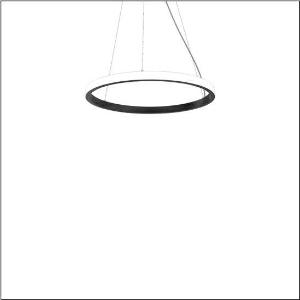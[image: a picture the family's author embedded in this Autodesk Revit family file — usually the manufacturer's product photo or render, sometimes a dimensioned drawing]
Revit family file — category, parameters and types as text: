
# Revit family: silica_21_ring-o_5pjbo2d3104a
name_source: partatom
category: Lighting Fixtures
units: mm (PartAtom-declared; Revit-internal decimal feet)

## family parameters
Cut with Voids When Loaded = No
Host = Face
Light Source = No
Part Type = Normal
Room Calculation Point = No
Round Connector Dimension = Use Diameter
Shared = No

## types (1)
- Silica 21 Ring-O (1 x LED, 4940 lm, 80 W, 4000K)
    Apparent Load = 80 VA
    CIE Flux Codes = 2 16 49 50 100
    Color Rendering = 80
    Color Temperature = 4000K
    Default Elevation = 1800 mm
    Description = Silica 21 Ring-O, suspended luminaire, of PMMA, frosted, light emission: outer ring side luminous distribution, primary light characteristic: symmetric, installation type: suspended mounting, LED, rated luminous flux: 4.940lm, luminous efficacy: 62lm/W, light colour: 840, colour temperature: 4000K, control gear: DALI 2, with terminal, 5-pole, mains connection: 230V, AC/DC, 0/50..60Hz, rated input power: 80W, housing, of extruded aluminium section, jet black (RAL 9005), diameter: 810mm, ceiling canopy, jet black (RAL 9005), protection rating (lamp compartment): IP40, insulation class (complete): insulation class I (protective earthing), certification: CE, impact resistance: IK02, permissible operating ambient temperature: 0..+35°C, packaging unit: 1 piece
    Height = 48 mm  [stored 0.15748 ft]
    Lamp = 1 x LED
    Lamp Light Flux = 4940 lm
    Lamp Power = 80 W
    Lamp count = 1
    Length = 810 mm
    Luminous efficacy = 62 lm/W
    Manufacturer = Siteco
    ModVariant = No
    Model = 5PJBO2D3104A
    Mounting Place = Ceiling
    Mounting Type = Pendant
    Number of Poles = 1
    OnlyDefault = Yes
    Power Factor = 1
    Product Name = Silica 21 Ring-O
    Product group = suspended luminaire
    ProductGroupID = 904
    Protection Class = Protection class I
    Protection Degree = IP 40
    RLX_Detail_Level = 1
    RLX_Emergency_Light_Flux = 0 lm
    RLX_Emergency_Type = 0
    RLX_Emergency_Type_DB = No
    RlxData = <blob elided: 14065 chars, md5=9f3827fa>
    Socket = socket
    Standby Power = 0 W
    System Light Flux = 4940 lm
    System Power = 80 W
    Type Comments = Product without accessories
    Type Image = l_1258381.jpg
    URL = http://relux.com
    VarID = ---
    Voltage = 0 V
    Weight = 0.00 kg
    Width = 0 mm  [stored 0 ft]

note: [stored X ft] marks values corroborated as IEEE doubles in the binary element streams (Revit-internal decimal feet)

## geometry (parser evidence)
native form markers: Sweep x11
no freeform markers — native parametric forms only
